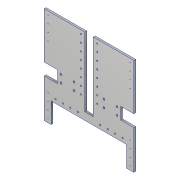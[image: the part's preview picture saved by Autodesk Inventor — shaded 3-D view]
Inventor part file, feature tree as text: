
AUTODESK INVENTOR PART (.ipt)
format: ipt  version: 2018 (Build 220112000, 112)  size: 276,992 bytes
history: native  units: in
note: dims shown in document units (in); Inventor stores cm internally (conversion verified against a paired STEP export)
features: reference x11, sketch x10, extrude x7, other x5, hole x4
ambient origin geometry x8: Origin, YZ Plane, XZ Plane, XY Plane, X Axis, Y Axis, Z Axis, Center Point
bodies: Solid1 (feature_tree)
feature tree (37):
  extrude  "Extrusion1"  Depth=13.0in
  extrude  "Extrusion2"  Depth=0.25in TaperAngle=0.0deg
  hole  "Hole1"  [1 undecoded]
  hole  "Hole2"  [1 undecoded]
  extrude  "Extrusion3"  Depth=0.0625in
  extrude  "Extrusion4"  Depth=3.75in
  extrude  "Extrusion5"  Depth=4.0in
  extrude  "Extrusion6"  TaperAngle=0.0deg  [1 undecoded]
  hole  "Hole3"  [1 undecoded]
  extrude  "Extrusion8"  Depth=0.25in TaperAngle=0.0deg
  hole  "Hole4"  [1 undecoded]
  sketch  "Sketch1"  dims[d0=12.0in d1=13.0in]
  sketch  "Sketch2"  dims[d2=0.25in d3=0.0in d4=0.25in d5=0.0in]
  reference  "Reference1"
  sketch  "Sketch3"  dims[d6=0.25in d7=0.75in d8=0.375in d9=0.25in d10=0.5635in d11=1.0in d12=0.8108in]
  reference  "Reference2"
  reference  "Reference3"
  sketch  "Sketch5"  dims[d13=0.07in d14=0.75in d15=0.119in d16=0.25in d17=0.5635in d18=1.0in d19=0.8108in d20=0.0in]
  reference  "Reference4"
  reference  "Reference5"
  sketch  "Sketch6"  dims[d21=3.0in d22=0.25in d23=0.0in]
  sketch  "Sketch7"  dims[d24=0.0625in d25=0.0625in]
  reference  "Reference6"
  reference  "Reference7"
  reference  "Reference8"
  sketch  "Sketch8"  dims[d26=0.25in d27=0.0in d28=3.75in]
  sketch  "Sketch10"  dims[d29=0.0in d30=4.0in]
  reference  "Reference9"
  sketch  "Sketch11"  dims[d31=0.25in d32=0.0in d33=0.0in]
  reference  "Reference10"
  sketch  "Sketch12"  dims[d34=0.0in d35=0.25in d36=0.0in d43=0.177in d44=0.75in d45=0.332in d46=0.25in d47=0.5635in d48=1.0in d49=0.8108in d50=0.25in d51=0.0in d52=0.177in d53=0.75in d54=0.332in d55=0.25in d56=0.5635in d57=1.0in d58=0.8108in]
  reference  "Reference11"
  parser-record x1  (decoder bookkeeping rows leaked as tree rows — omitted from the tree; the rows remain in map.json)
  other  "Robot.iam"
  other  "Piv Pannel 2:1"
  other  "Support Pivs 25 uppereeeeee:1"
  other  "Support Pivs 25 middle:1"
note: 5 required parameter values undecoded (feature->parameter linkage not recoverable at this tier; creation-order binding heuristic only, values carry confidence <= 0.55)
note: 1 file-system path scrubbed to <path> (originals preserved in map.json)
